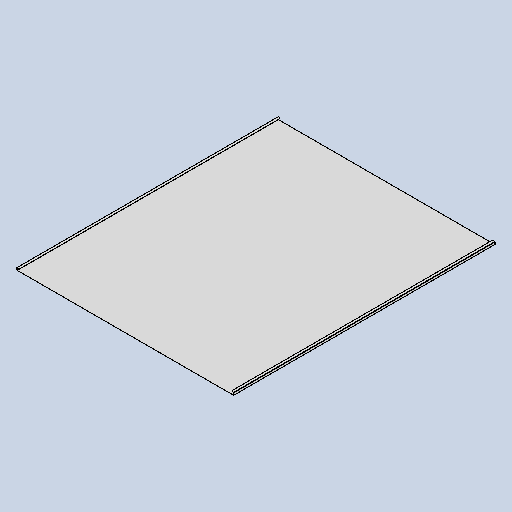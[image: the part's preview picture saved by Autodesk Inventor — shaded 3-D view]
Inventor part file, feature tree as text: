
AUTODESK INVENTOR PART (.ipt)
format: ipt  version: 2025 (Build 290162010, 162A)  size: 195,072 bytes
history: native  units: mm
features: sheet_metal_op x13, other x6, sketch x5, chamfer x4
ambient origin geometry x8: Origin, YZ Plane, XZ Plane, XY Plane, X Axis, Y Axis, Z Axis, Center Point
bodies: Body1 (feature_tree)
feature tree (28):
  sheet_metal_op  "Face1"
  sheet_metal_op  "Flange2"
  sheet_metal_op  "Flange3"
  sheet_metal_op  "Flange4"
  sheet_metal_op  "Flange5"
  chamfer  "Corner Round1"
  chamfer  "Corner Round2"
  chamfer  "Corner Round3"
  chamfer  "Corner Round4"
  sketch  "Sketch6"  dims[d12=23.212879mm]
  other  "Plate2"
  sketch  "Sketch11"  dims[d52=814.2mm]
  other  "Plate4"
  sheet_metal_op  "Bend3"
  sheet_metal_op  "Corner3"
  sketch  "Sketch12"  dims[d53=980.0mm]
  other  "Plate5"
  sheet_metal_op  "Bend4"
  sheet_metal_op  "Corner4"
  sketch  "Sketch13"  dims[d54=0.5mm]
  other  "Plate6"
  sheet_metal_op  "Bend5"
  sheet_metal_op  "Corner5"
  sketch  "Sketch14"  dims[d84=0.5mm d85=0.25mm d86=1.0mm d87=0.5mm d88=10.0mm d89=90.0deg d90=0.5mm d91=2.0mm d92=0.5mm d93=0.5mm d94=0.5mm d95=0.25mm d96=1.0mm d97=0.5mm d98=10.0mm d99=90.0deg d100=0.5mm d101=2.0mm d102=0.5mm d103=0.5mm d104=0.5mm d105=0.25mm d106=1.0mm d107=0.5mm d108=10.0mm d109=90.0deg d110=0.5mm d111=2.0mm d112=0.5mm d113=0.5mm d114=0.5mm d115=0.25mm d116=1.0mm d117=0.5mm d118=10.0mm d119=90.0deg d120=0.5mm d121=2.0mm d122=0.5mm d123=0.5mm d124=4.0mm d125=4.0mm d126=4.0mm d127=4.0mm]
  other  "Plate7"
  sheet_metal_op  "Bend6"
  sheet_metal_op  "Corner6"
  other  "Definition1"
